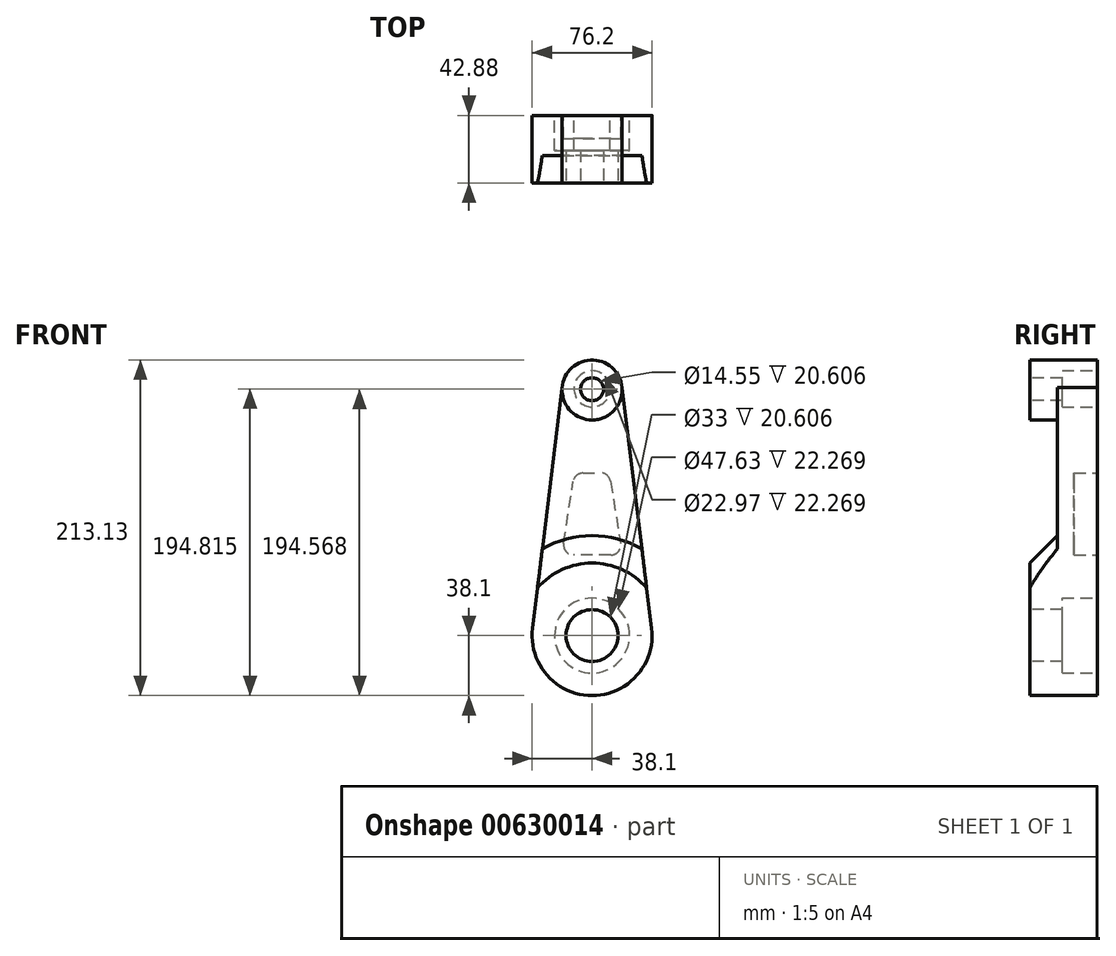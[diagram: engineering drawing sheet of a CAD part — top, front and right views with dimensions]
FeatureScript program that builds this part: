
annotation { "Feature Type Name" : "Feature", "Feature Type Description" : "" }
export const myFeature = defineFeature(function(context is Context, id is Id, definition is map)
    precondition{}
    {
        {
            var Q0;
            Q0=qCreatedBy(makeId("Front.planeOp"),FACE);
            var sketch = newSketch(context, id + "F0", { "sketchPlane" : qUnion([Q0])});
            skCircle(sketch, "E0", {"center": v(0, 0) * mm, "radius": 38.1 * mm});
            skCircle(sketch, "E1", {"center": v(0, 155.98) * mm, "radius": 19.05 * mm});
            skLineSegment(sketch, "E2", {"start": v(-19, 157.35) * mm, "end": v(-38.39, 0) * mm});
            skLineSegment(sketch, "E3", {"start": v(-38.39, 0) * mm, "end": v(-38.39, 0) * mm});
            skLineSegment(sketch, "E4", {"start": v(18.98, 157.57) * mm, "end": v(38.39, 0) * mm});
            skLineSegment(sketch, "E5", {"start": v(38.39, 0) * mm, "end": v(38.39, 0) * mm});
            skSolve(sketch);
        }
        {
            var Q0;
            {var subQ0=sQuery(id+"F0.wireOp",EDGE,"E2");var subQ1=sQuery(id+"F0.wireOp",EDGE,"E0");var subQ2=makeQuery(id+"F0.imprint","INTERSECT",VERTEX,{"derivedFrom":[subQ1,subQ0]});Q0=makeQuery(id+"F0.imprint","IMPRINT",FACE,{"disambiguationData":[TD([[makeQuery(id+"F0.imprint","IMPRINT",EDGE,{"disambiguationData":[TD([[subQ2,1.0]])],"derivedFrom":subQ1}),-1.0]])]});}
            var Q1;
            {var subQ0=sQuery(id+"F0.wireOp",EDGE,"E1");var subQ1=makeQuery(id+"F0.imprint","INTERSECT",VERTEX,{"derivedFrom":[subQ0,sQuery(id+"F0.wireOp",EDGE,"E2")]});Q1=makeQuery(id+"F0.imprint","IMPRINT",FACE,{"disambiguationData":[TD([[makeQuery(id+"F0.imprint","IMPRINT",EDGE,{"disambiguationData":[TD([[subQ1,1.0]])],"derivedFrom":subQ0}),1.0]])]});}
            var Q2;
            {var subQ0=sQuery(id+"F0.wireOp",EDGE,"E0");var subQ1=makeQuery(id+"F0.imprint","INTERSECT",VERTEX,{"derivedFrom":[subQ0,sQuery(id+"F0.wireOp",EDGE,"E2")]});Q2=makeQuery(id+"F0.imprint","IMPRINT",FACE,{"disambiguationData":[TD([[makeQuery(id+"F0.imprint","IMPRINT",EDGE,{"disambiguationData":[TD([[subQ1,1.0]])],"derivedFrom":subQ0}),1.0]])]});}
            extrude(context, id + "F1", {"entities" : qUnion([Q0, Q1, Q2]), "depth" : 25.4 * mm, "offsetDistance" : 25.4 * mm});
        }
        {
            var Q0;
            {var subQ0=sQuery(id+"F0.wireOp",EDGE,"E1");var subQ1=makeQuery(id+"F0.imprint","INTERSECT",VERTEX,{"derivedFrom":[subQ0,sQuery(id+"F0.wireOp",EDGE,"E2")]});Q0=makeQuery(id+"F0.imprint","IMPRINT",FACE,{"disambiguationData":[TD([[makeQuery(id+"F0.imprint","IMPRINT",EDGE,{"disambiguationData":[TD([[subQ1,1.0]])],"derivedFrom":subQ0}),1.0]])]});}
            var Q1;
            {var subQ0=sQuery(id+"F0.wireOp",EDGE,"E0");var subQ1=makeQuery(id+"F0.imprint","INTERSECT",VERTEX,{"derivedFrom":[subQ0,sQuery(id+"F0.wireOp",EDGE,"E2")]});Q1=makeQuery(id+"F0.imprint","IMPRINT",FACE,{"disambiguationData":[TD([[makeQuery(id+"F0.imprint","IMPRINT",EDGE,{"disambiguationData":[TD([[subQ1,1.0]])],"derivedFrom":subQ0}),1.0]])]});}
            extrude(context, id + "F2", {"entities" : qUnion([Q0, Q1]), "operationType" : NewBodyOperationType.ADD, "depth" : 42.88 * mm, "offsetDistance" : 25.4 * mm});
        }
        {
            var Q0;
            {var subQ0=sQuery(id+"F0.wireOp",EDGE,"E0");Q0=makeQuery(id+"F2.boolean.opBoolean","INTERSECT",EDGE,{"derivedFrom":[makeQuery(id+"F1.opExtrude","CAP_FACE",FACE,{"disambiguationData":[OSD([subQ0,sQuery(id+"F0.wireOp",EDGE,"E1"),sQuery(id+"F0.wireOp",EDGE,"E2"),sQuery(id+"F0.wireOp",EDGE,"E4")])],"isStart":false}),makeQuery(id+"F2.opExtrude","SWEPT_FACE",FACE,{"disambiguationData":[OSD([subQ0])]})]});}
            chamfer(context, id + "F3", {"entities" : qUnion([Q0]), "width" : 25.4 * mm, "tangentPropagation" : true});
        }
        {
            var Q0;
            Q0=qCreatedBy(makeId("Front.planeOp"),FACE);
            var sketch = newSketch(context, id + "F4", { "sketchPlane" : qUnion([Q0])});
            skCircle(sketch, "E6", {"center": v(0, 156.47) * mm, "radius": 7.27 * mm});
            skCircle(sketch, "E7", {"center": v(0, 0) * mm, "radius": 16.5 * mm});
            skSolve(sketch);
        }
        {
            var Q0;
            Q0 = qSketchRegion(id + "F4", true);
            extrude(context, id + "F5", {"entities" : qUnion([Q0]), "operationType" : NewBodyOperationType.REMOVE, "endBound" : BoundingType.SYMMETRIC, "oppositeDirection" : true, "depth" : 129.8 * mm, "offsetDistance" : 25.4 * mm});
        }
        {
            var Q0;
            Q0=qCreatedBy(makeId("Front.planeOp"),FACE);
            var sketch = newSketch(context, id + "F6", { "sketchPlane" : qUnion([Q0])});
            skCircle(sketch, "E8", {"center": v(0, 156.71) * mm, "radius": 11.49 * mm});
            skCircle(sketch, "E9", {"center": v(0, 0) * mm, "radius": 23.82 * mm});
            skSolve(sketch);
        }
        {
            var Q0;
            Q0 = qSketchRegion(id + "F6", true);
            extrude(context, id + "F7", {"entities" : qUnion([Q0]), "operationType" : NewBodyOperationType.REMOVE, "depth" : 22.27 * mm, "offsetDistance" : 25.4 * mm});
        }
        {
            var Q0;
            Q0=qCreatedBy(makeId("Front.planeOp"),FACE);
            var sketch = newSketch(context, id + "F8", { "sketchPlane" : qUnion([Q0])});
            skLineSegment(sketch, "E10", {"start": v(11.6, 98.1) * mm, "end": v(18.15, 58.55) * mm});
            skLineSegment(sketch, "E11", {"start": v(11.89, 51.16) * mm, "end": v(-11.74, 51.16) * mm});
            skLineSegment(sketch, "E12", {"start": v(-18.02, 58.46) * mm, "end": v(-12.04, 97.82) * mm});
            skLineSegment(sketch, "E13", {"start": v(-5.87, 103.21) * mm, "end": v(5.22, 103.41) * mm});
            skPoint(sketch, "E14.visualSharp", {"position": v(10.7, 103.51) * mm});
            skArc(sketch, "E14.filletArc", {"start": v(11.6, 98.1) * mm, "mid": v(9.4, 101.94) * mm, "end": v(5.22, 103.41) * mm});
            skPoint(sketch, "E15.visualSharp", {"position": v(-11.23, 103.12) * mm});
            skArc(sketch, "E15.filletArc", {"start": v(-5.87, 103.21) * mm, "mid": v(-9.94, 101.64) * mm, "end": v(-12.04, 97.82) * mm});
            skPoint(sketch, "E16.visualSharp", {"position": v(19.38, 51.16) * mm});
            skArc(sketch, "E16.filletArc", {"start": v(11.89, 51.16) * mm, "mid": v(16.73, 53.4) * mm, "end": v(18.15, 58.55) * mm});
            skPoint(sketch, "E17.visualSharp", {"position": v(-19.13, 51.16) * mm});
            skArc(sketch, "E17.filletArc", {"start": v(-18.02, 58.46) * mm, "mid": v(-16.56, 53.37) * mm, "end": v(-11.74, 51.16) * mm});
            skSolve(sketch);
        }
        {
            var Q0;
            Q0=makeQuery(id+"F8.imprint","IMPRINT",FACE,{"disambiguationData":[TD([[makeQuery(id+"F8.imprint","IMPRINT",EDGE,{"derivedFrom":sQuery(id+"F8.wireOp",EDGE,"E10")}),-1.0]])]});
            extrude(context, id + "F9", {"entities" : qUnion([Q0]), "operationType" : NewBodyOperationType.REMOVE, "depth" : 14.78 * mm, "offsetDistance" : 25.4 * mm});
        }
    });
